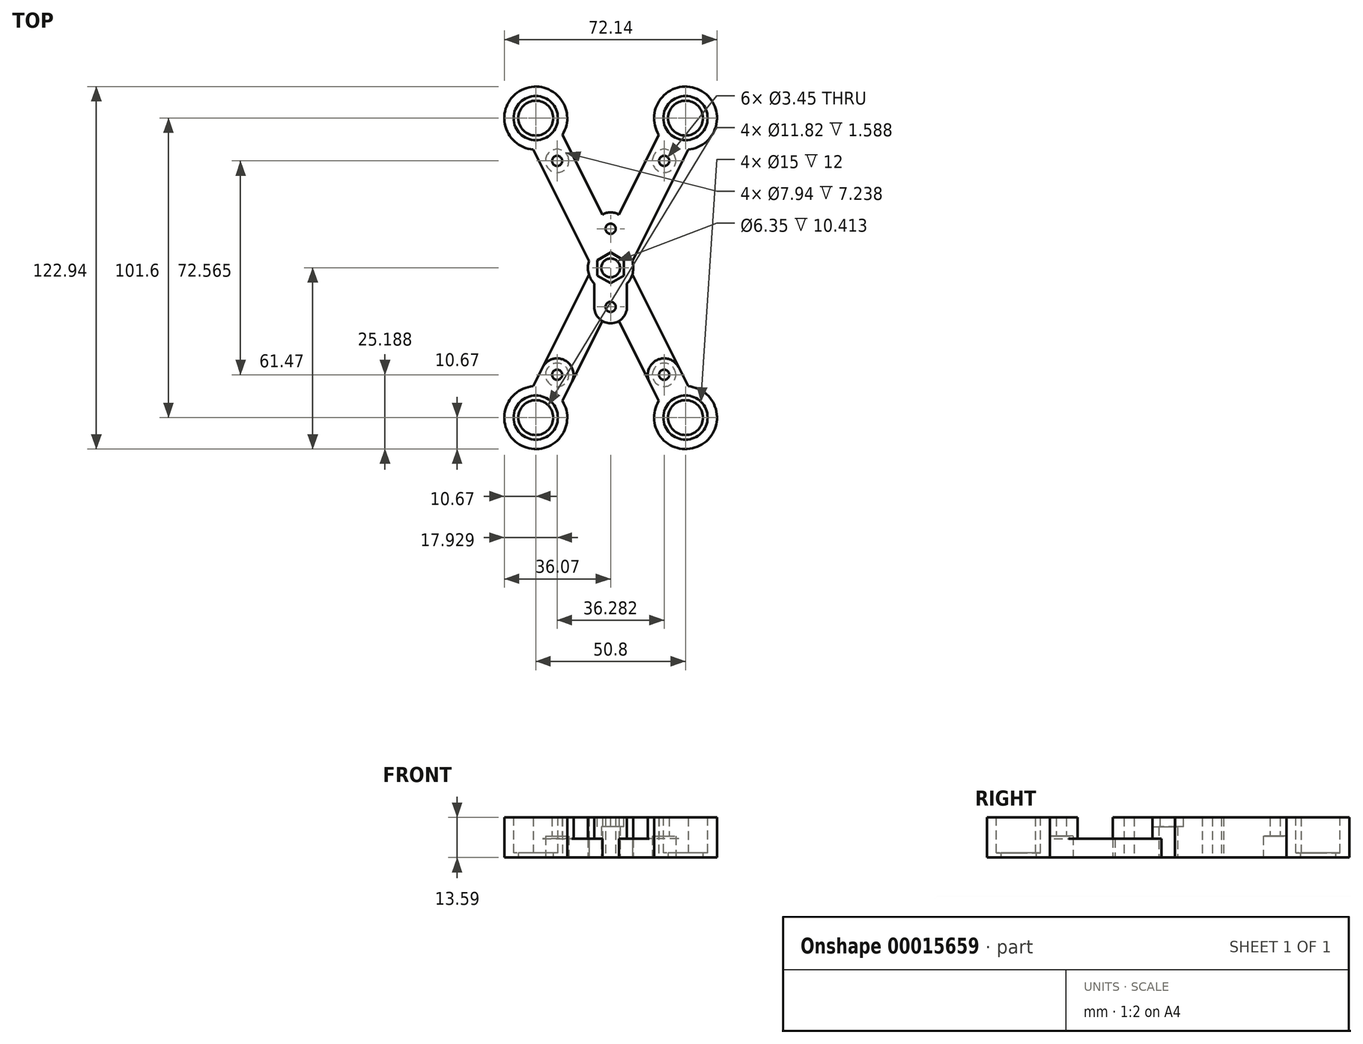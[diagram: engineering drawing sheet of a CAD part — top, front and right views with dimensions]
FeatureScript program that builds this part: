
annotation { "Feature Type Name" : "Feature", "Feature Type Description" : "" }
export const myFeature = defineFeature(function(context is Context, id is Id, definition is map)
    precondition{}
    {
        {
            var Q0;
            Q0=qCreatedBy(makeId("Top.planeOp"),FACE);
            var sketch = newSketch(context, id + "F0", { "sketchPlane" : qUnion([Q0])});
            skCircle(sketch, "E0", {"center": v(0, 0) * mm, "radius": 3.18 * mm});
            skLineSegment(sketch, "E1.rect.bottom", {"start": v(-25.4, 50.8) * mm, "end": v(25.4, 50.8) * mm, "construction": true});
            skLineSegment(sketch, "E1.rect.top", {"start": v(-25.4, -50.8) * mm, "end": v(25.4, -50.8) * mm, "construction": true});
            skLineSegment(sketch, "E1.rect.left", {"start": v(-25.4, 50.8) * mm, "end": v(-25.4, -50.8) * mm, "construction": true});
            skLineSegment(sketch, "E1.rect.right", {"start": v(25.4, 50.8) * mm, "end": v(25.4, -50.8) * mm, "construction": true});
            skCircle(sketch, "E2", {"center": v(-25.4, 50.8) * mm, "radius": 5.91 * mm});
            skCircle(sketch, "E3", {"center": v(-25.4, -50.8) * mm, "radius": 5.91 * mm});
            skCircle(sketch, "E4", {"center": v(25.4, -50.8) * mm, "radius": 5.91 * mm});
            skCircle(sketch, "E5", {"center": v(25.4, 50.8) * mm, "radius": 5.91 * mm});
            skArc(sketch, "E6", {"start": v(-16.35, 45.13) * mm, "mid": v(-30.17, 60.35) * mm, "end": v(-26.3, 40.16) * mm});
            skArc(sketch, "E7", {"start": v(26.3, 40.16) * mm, "mid": v(30.17, 60.35) * mm, "end": v(16.35, 45.13) * mm});
            skArc(sketch, "E8", {"start": v(-26.3, -40.16) * mm, "mid": v(-30.17, -60.35) * mm, "end": v(-16.35, -45.13) * mm});
            skArc(sketch, "E9", {"start": v(16.35, -45.13) * mm, "mid": v(30.17, -60.35) * mm, "end": v(26.3, -40.16) * mm});
            skLineSegment(sketch, "E10", {"start": v(0, 0) * mm, "end": v(18.14, 36.28) * mm, "construction": true});
            skLineSegment(sketch, "E11", {"start": v(0, 0) * mm, "end": v(18.14, -36.28) * mm, "construction": true});
            skLineSegment(sketch, "E12", {"start": v(-26.3, 40.16) * mm, "end": v(-16.35, 45.13) * mm, "construction": true});
            skLineSegment(sketch, "E13", {"start": v(-26.3, -40.16) * mm, "end": v(-16.35, -45.13) * mm, "construction": true});
            skLineSegment(sketch, "E14", {"start": v(16.35, -45.13) * mm, "end": v(26.3, -40.16) * mm, "construction": true});
            skPoint(sketch, "E15", {"position": v(-21.32, 42.65) * mm});
            skPoint(sketch, "E16", {"position": v(-21.32, -42.65) * mm});
            skPoint(sketch, "E17", {"position": v(21.32, -42.65) * mm});
            skPoint(sketch, "E18", {"position": v(21.32, 42.65) * mm});
            skLineSegment(sketch, "E19", {"start": v(25.4, -50.8) * mm, "end": v(18.14, -36.28) * mm, "construction": true});
            skLineSegment(sketch, "E20", {"start": v(25.4, 50.8) * mm, "end": v(18.14, 36.28) * mm, "construction": true});
            skArc(sketch, "E21", {"start": v(26.3, -40.16) * mm, "mid": v(20.63, -41.25) * mm, "end": v(16.35, -45.13) * mm, "construction": true});
            skCircle(sketch, "E22", {"center": v(18.14, -36.28) * mm, "radius": 5.56 * mm, "construction": true});
            skLineSegment(sketch, "E23", {"start": v(16.35, -45.13) * mm, "end": v(2.81, -18.04) * mm});
            skLineSegment(sketch, "E24", {"start": v(26.3, -40.16) * mm, "end": v(7.35, -2.28) * mm});
            skLineSegment(sketch, "E25", {"start": v(-25.4, 50.8) * mm, "end": v(-18.14, 36.28) * mm, "construction": true});
            skLineSegment(sketch, "E26", {"start": v(-18.14, 36.28) * mm, "end": v(0, 0) * mm, "construction": true});
            skLineSegment(sketch, "E27", {"start": v(0, 0) * mm, "end": v(-18.14, -36.28) * mm, "construction": true});
            skLineSegment(sketch, "E28", {"start": v(-18.14, -36.28) * mm, "end": v(-25.4, -50.8) * mm, "construction": true});
            skLineSegment(sketch, "E29", {"start": v(-16.35, -45.13) * mm, "end": v(-2.81, -18.04) * mm});
            skLineSegment(sketch, "E30", {"start": v(-26.3, -40.16) * mm, "end": v(-7.35, -2.28) * mm});
            skLineSegment(sketch, "E31", {"start": v(-26.3, 40.16) * mm, "end": v(-7.35, 2.28) * mm});
            skLineSegment(sketch, "E32", {"start": v(-16.35, 45.13) * mm, "end": v(-2.81, 18.04) * mm});
            skLineSegment(sketch, "E33", {"start": v(16.35, 45.13) * mm, "end": v(26.3, 40.16) * mm, "construction": true});
            skLineSegment(sketch, "E34", {"start": v(16.35, 45.13) * mm, "end": v(2.81, 18.04) * mm});
            skLineSegment(sketch, "E35", {"start": v(26.3, 40.16) * mm, "end": v(7.35, 2.28) * mm});
            skCircle(sketch, "E36", {"center": v(-18.14, -36.28) * mm, "radius": 1.73 * mm});
            skCircle(sketch, "E37", {"center": v(18.14, -36.28) * mm, "radius": 1.73 * mm});
            skCircle(sketch, "E38", {"center": v(18.14, 36.28) * mm, "radius": 1.73 * mm});
            skCircle(sketch, "E39", {"center": v(-18.14, 36.28) * mm, "radius": 1.73 * mm});
            skCircle(sketch, "E40", {"center": v(0, 0) * mm, "radius": 7.7 * mm, "construction": true});
            skLineSegment(sketch, "E41", {"start": v(0, -13.25) * mm, "end": v(0, 13.25) * mm, "construction": true});
            skArc(sketch, "E42", {"start": v(2.81, 18.04) * mm, "mid": v(0, 18.8) * mm, "end": v(-2.81, 18.04) * mm});
            skArc(sketch, "E43", {"start": v(-2.81, 18.04) * mm, "mid": v(0, 7.7) * mm, "end": v(2.81, 18.04) * mm, "construction": true});
            skCircle(sketch, "E44", {"center": v(0, 13.25) * mm, "radius": 1.73 * mm});
            skCircle(sketch, "E45", {"center": v(0, -13.25) * mm, "radius": 1.73 * mm});
            skArc(sketch, "E46", {"start": v(-2.81, -18.04) * mm, "mid": v(0, -18.8) * mm, "end": v(2.81, -18.04) * mm});
            skArc(sketch, "E47", {"start": v(7.35, -2.28) * mm, "mid": v(7.7, 0) * mm, "end": v(7.35, 2.28) * mm});
            skArc(sketch, "E48", {"start": v(-7.35, 2.28) * mm, "mid": v(-7.7, 0) * mm, "end": v(-7.35, -2.28) * mm});
            skSolve(sketch);
        }
        {
            var Q0;
            Q0 = qSketchRegion(id + "F0", true);
            extrude(context, id + "F1", {"entities" : qUnion([Q0]), "depth" : 13.6 * mm});
        }
        {
            var Q0;
            Q0=makeQuery(id+"F1.opExtrude","CAP_FACE",FACE,{"disambiguationData":[OSD([sQuery(id+"F0.wireOp",EDGE,"E0"),sQuery(id+"F0.wireOp",EDGE,"E2"),sQuery(id+"F0.wireOp",EDGE,"E3"),sQuery(id+"F0.wireOp",EDGE,"E4"),sQuery(id+"F0.wireOp",EDGE,"E5"),sQuery(id+"F0.wireOp",EDGE,"E6"),sQuery(id+"F0.wireOp",EDGE,"E7"),sQuery(id+"F0.wireOp",EDGE,"E8"),sQuery(id+"F0.wireOp",EDGE,"E9"),sQuery(id+"F0.wireOp",EDGE,"E23"),sQuery(id+"F0.wireOp",EDGE,"E24"),sQuery(id+"F0.wireOp",EDGE,"E29"),sQuery(id+"F0.wireOp",EDGE,"E30"),sQuery(id+"F0.wireOp",EDGE,"E31"),sQuery(id+"F0.wireOp",EDGE,"E32"),sQuery(id+"F0.wireOp",EDGE,"E34"),sQuery(id+"F0.wireOp",EDGE,"E35"),sQuery(id+"F0.wireOp",EDGE,"E36"),sQuery(id+"F0.wireOp",EDGE,"E37"),sQuery(id+"F0.wireOp",EDGE,"E38"),sQuery(id+"F0.wireOp",EDGE,"E39")])],"isStart":false});
            var sketch = newSketch(context, id + "F2", { "sketchPlane" : qUnion([Q0])});
            skCircle(sketch, "E49.cCircle", {"center": v(0, 0) * mm, "radius": 4.52 * mm, "construction": true});
            skLineSegment(sketch, "E49.0", {"start": v(-4.52, -2.61) * mm, "end": v(-4.52, 2.61) * mm});
            skLineSegment(sketch, "E49.1", {"start": v(-4.52, 2.61) * mm, "end": v(0, 5.22) * mm});
            skLineSegment(sketch, "E49.2", {"start": v(0, 5.22) * mm, "end": v(4.52, 2.61) * mm});
            skLineSegment(sketch, "E49.3", {"start": v(4.52, 2.61) * mm, "end": v(4.52, -2.61) * mm});
            skLineSegment(sketch, "E49.4", {"start": v(4.52, -2.61) * mm, "end": v(0, -5.22) * mm});
            skLineSegment(sketch, "E49.5", {"start": v(0, -5.22) * mm, "end": v(-4.52, -2.61) * mm});
            skPoint(sketch, "E49.0.midPoint", {"position": v(-4.52, 0) * mm});
            skSolve(sketch);
        }
        {
            var Q0;
            Q0 = qSketchRegion(id + "F2", true);
            extrude(context, id + "F3", {"entities" : qUnion([Q0]), "operationType" : NewBodyOperationType.REMOVE, "oppositeDirection" : true, "depth" : 3.17 * mm});
        }
        {
            var Q0;
            Q0=makeQuery(id+"F1.opExtrude","CAP_FACE",FACE,{"disambiguationData":[OSD([sQuery(id+"F0.wireOp",EDGE,"E0"),sQuery(id+"F0.wireOp",EDGE,"E2"),sQuery(id+"F0.wireOp",EDGE,"E3"),sQuery(id+"F0.wireOp",EDGE,"E4"),sQuery(id+"F0.wireOp",EDGE,"E5"),sQuery(id+"F0.wireOp",EDGE,"E6"),sQuery(id+"F0.wireOp",EDGE,"E7"),sQuery(id+"F0.wireOp",EDGE,"E8"),sQuery(id+"F0.wireOp",EDGE,"E9"),sQuery(id+"F0.wireOp",EDGE,"E23"),sQuery(id+"F0.wireOp",EDGE,"E24"),sQuery(id+"F0.wireOp",EDGE,"E29"),sQuery(id+"F0.wireOp",EDGE,"E30"),sQuery(id+"F0.wireOp",EDGE,"E31"),sQuery(id+"F0.wireOp",EDGE,"E32"),sQuery(id+"F0.wireOp",EDGE,"E34"),sQuery(id+"F0.wireOp",EDGE,"E35"),sQuery(id+"F0.wireOp",EDGE,"E36"),sQuery(id+"F0.wireOp",EDGE,"E37"),sQuery(id+"F0.wireOp",EDGE,"E38"),sQuery(id+"F0.wireOp",EDGE,"E39")])],"isStart":false});
            var sketch = newSketch(context, id + "F4", { "sketchPlane" : qUnion([Q0])});
            skCircle(sketch, "E50", {"center": v(-25.4, -50.8) * mm, "radius": 7.5 * mm});
            skCircle(sketch, "E51", {"center": v(-25.4, 50.8) * mm, "radius": 7.5 * mm});
            skCircle(sketch, "E52", {"center": v(25.4, 50.8) * mm, "radius": 7.5 * mm});
            skCircle(sketch, "E53", {"center": v(25.4, -50.8) * mm, "radius": 7.5 * mm});
            skSolve(sketch);
        }
        {
            var Q0;
            Q0 = qSketchRegion(id + "F4", true);
            extrude(context, id + "F5", {"entities" : qUnion([Q0]), "operationType" : NewBodyOperationType.REMOVE, "oppositeDirection" : true, "depth" : 12 * mm});
        }
        {
            var Q0;
            Q0=makeQuery(id+"F1.opExtrude","CAP_FACE",FACE,{"disambiguationData":[OSD([sQuery(id+"F0.wireOp",EDGE,"E0"),sQuery(id+"F0.wireOp",EDGE,"E2"),sQuery(id+"F0.wireOp",EDGE,"E3"),sQuery(id+"F0.wireOp",EDGE,"E4"),sQuery(id+"F0.wireOp",EDGE,"E5"),sQuery(id+"F0.wireOp",EDGE,"E6"),sQuery(id+"F0.wireOp",EDGE,"E7"),sQuery(id+"F0.wireOp",EDGE,"E8"),sQuery(id+"F0.wireOp",EDGE,"E9"),sQuery(id+"F0.wireOp",EDGE,"E23"),sQuery(id+"F0.wireOp",EDGE,"E24"),sQuery(id+"F0.wireOp",EDGE,"E29"),sQuery(id+"F0.wireOp",EDGE,"E30"),sQuery(id+"F0.wireOp",EDGE,"E31"),sQuery(id+"F0.wireOp",EDGE,"E32"),sQuery(id+"F0.wireOp",EDGE,"E34"),sQuery(id+"F0.wireOp",EDGE,"E35"),sQuery(id+"F0.wireOp",EDGE,"E36"),sQuery(id+"F0.wireOp",EDGE,"E37"),sQuery(id+"F0.wireOp",EDGE,"E38"),sQuery(id+"F0.wireOp",EDGE,"E39")])],"isStart":true});
            var sketch = newSketch(context, id + "F6", { "sketchPlane" : qUnion([Q0])});
            skCircle(sketch, "E54", {"center": v(18.14, 36.28) * mm, "radius": 3.97 * mm});
            skCircle(sketch, "E55", {"center": v(-18.14, 36.28) * mm, "radius": 3.97 * mm});
            skCircle(sketch, "E56", {"center": v(18.14, -36.28) * mm, "radius": 3.97 * mm});
            skCircle(sketch, "E57", {"center": v(-18.14, -36.28) * mm, "radius": 3.97 * mm});
            skSolve(sketch);
        }
        {
            var Q0;
            Q0 = qSketchRegion(id + "F6", true);
            extrude(context, id + "F7", {"entities" : qUnion([Q0]), "operationType" : NewBodyOperationType.REMOVE, "oppositeDirection" : true, "depth" : 7.24 * mm});
        }
        {
            var Q0;
            Q0=makeQuery(id+"F1.opExtrude","CAP_FACE",FACE,{"disambiguationData":[OSD([sQuery(id+"F0.wireOp",EDGE,"E0"),sQuery(id+"F0.wireOp",EDGE,"E2"),sQuery(id+"F0.wireOp",EDGE,"E3"),sQuery(id+"F0.wireOp",EDGE,"E4"),sQuery(id+"F0.wireOp",EDGE,"E5"),sQuery(id+"F0.wireOp",EDGE,"E6"),sQuery(id+"F0.wireOp",EDGE,"E7"),sQuery(id+"F0.wireOp",EDGE,"E8"),sQuery(id+"F0.wireOp",EDGE,"E9"),sQuery(id+"F0.wireOp",EDGE,"E23"),sQuery(id+"F0.wireOp",EDGE,"E24"),sQuery(id+"F0.wireOp",EDGE,"E29"),sQuery(id+"F0.wireOp",EDGE,"E30"),sQuery(id+"F0.wireOp",EDGE,"E31"),sQuery(id+"F0.wireOp",EDGE,"E32"),sQuery(id+"F0.wireOp",EDGE,"E34"),sQuery(id+"F0.wireOp",EDGE,"E35"),sQuery(id+"F0.wireOp",EDGE,"E36"),sQuery(id+"F0.wireOp",EDGE,"E37"),sQuery(id+"F0.wireOp",EDGE,"E38"),sQuery(id+"F0.wireOp",EDGE,"E39"),sQuery(id+"F0.wireOp",EDGE,"E42"),sQuery(id+"F0.wireOp",EDGE,"E44"),sQuery(id+"F0.wireOp",EDGE,"E45"),sQuery(id+"F0.wireOp",EDGE,"E46")])],"isStart":false});
            var sketch = newSketch(context, id + "F8", { "sketchPlane" : qUnion([Q0])});
            skArc(sketch, "E58", {"start": v(23.11, -33.8) * mm, "mid": v(15.66, -31.31) * mm, "end": v(13.17, -38.77) * mm});
            skArc(sketch, "E59", {"start": v(2.81, -18.04) * mm, "mid": v(4.82, -16.01) * mm, "end": v(5.56, -13.25) * mm});
            skLineSegment(sketch, "E60", {"start": v(5.56, -13.25) * mm, "end": v(5.56, -5.32) * mm});
            skArc(sketch, "E61", {"start": v(5.56, -5.32) * mm, "mid": v(6.63, -3.9) * mm, "end": v(7.35, -2.28) * mm});
            skLineSegment(sketch, "E62", {"start": v(0, -13.25) * mm, "end": v(0, 13.25) * mm, "construction": true});
            skLineSegment(sketch, "E63", {"start": v(13.17, -38.77) * mm, "end": v(2.81, -18.04) * mm});
            skLineSegment(sketch, "E64", {"start": v(7.35, -2.28) * mm, "end": v(23.11, -33.8) * mm});
            skArc(sketch, "E65", {"start": v(-13.17, -38.77) * mm, "mid": v(-15.66, -31.31) * mm, "end": v(-23.11, -33.8) * mm});
            skArc(sketch, "E66", {"start": v(-5.56, -13.25) * mm, "mid": v(-4.82, -16.01) * mm, "end": v(-2.81, -18.04) * mm});
            skArc(sketch, "E67", {"start": v(-7.35, -2.28) * mm, "mid": v(-6.63, -3.9) * mm, "end": v(-5.56, -5.32) * mm});
            skLineSegment(sketch, "E68", {"start": v(-5.56, -13.25) * mm, "end": v(-5.56, -5.32) * mm});
            skLineSegment(sketch, "E69", {"start": v(-2.81, -18.04) * mm, "end": v(-13.17, -38.77) * mm});
            skLineSegment(sketch, "E70", {"start": v(-23.11, -33.8) * mm, "end": v(-7.35, -2.28) * mm});
            skSolve(sketch);
        }
        {
            var Q0;
            Q0 = qSketchRegion(id + "F8", true);
            extrude(context, id + "F9", {"entities" : qUnion([Q0]), "operationType" : NewBodyOperationType.REMOVE, "oppositeDirection" : true, "depth" : 7.24 * mm});
        }
    });
